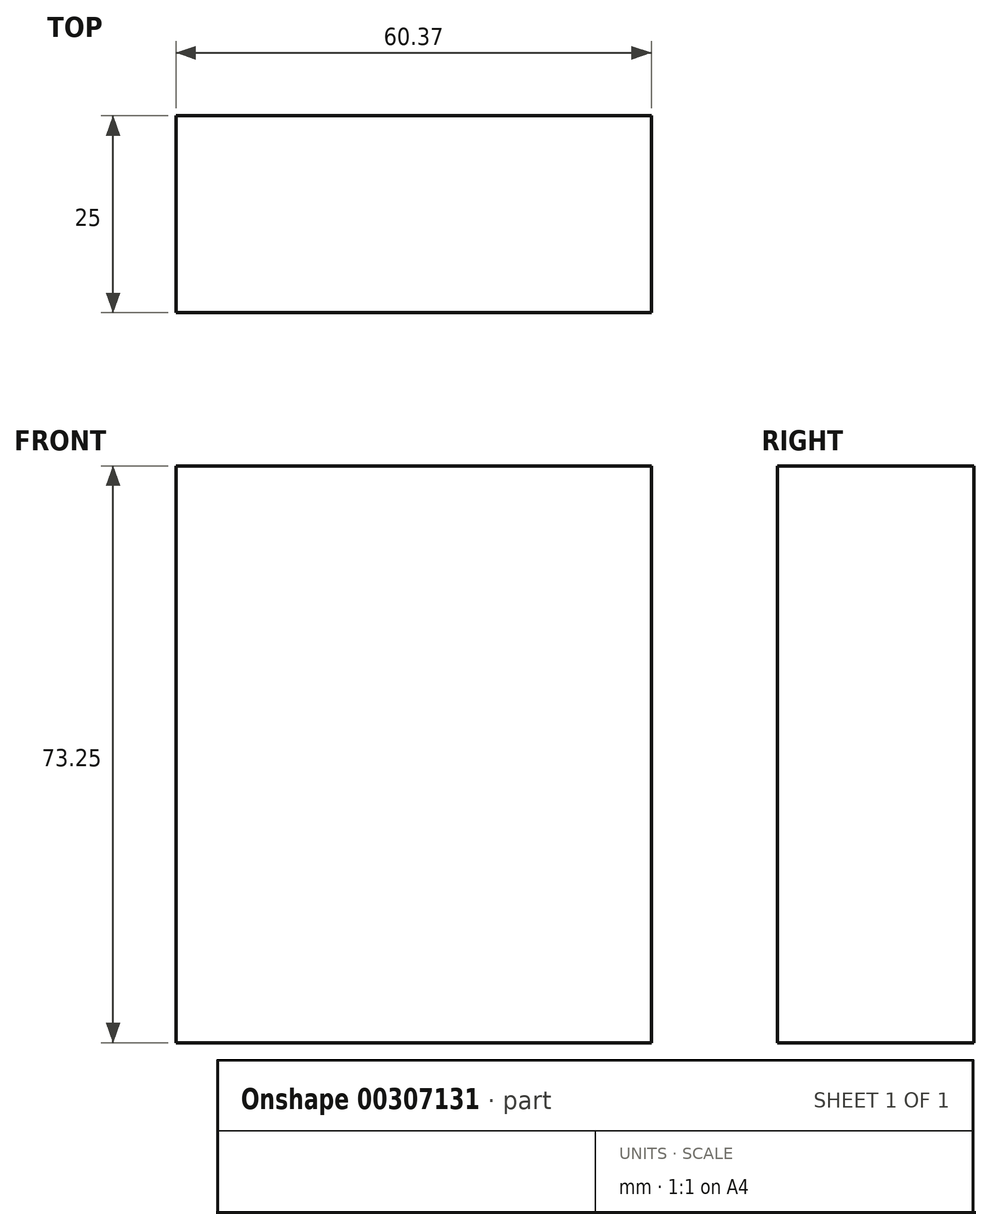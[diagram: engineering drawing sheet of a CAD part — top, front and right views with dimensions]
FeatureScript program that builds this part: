
annotation { "Feature Type Name" : "Feature", "Feature Type Description" : "" }
export const myFeature = defineFeature(function(context is Context, id is Id, definition is map)
    precondition{}
    {
        {
            var Q0;
            Q0=qCreatedBy(makeId("Front.planeOp"),FACE);
            var sketch = newSketch(context, id + "F0", { "sketchPlane" : qUnion([Q0])});
            skLineSegment(sketch, "E0.bottom", {"start": v(-95.1, 6.95) * mm, "end": v(-34.73, 6.95) * mm});
            skLineSegment(sketch, "E0.top", {"start": v(-95.1, 80.2) * mm, "end": v(-34.73, 80.2) * mm});
            skLineSegment(sketch, "E0.left", {"start": v(-95.1, 6.95) * mm, "end": v(-95.1, 80.2) * mm});
            skLineSegment(sketch, "E0.right", {"start": v(-34.73, 6.95) * mm, "end": v(-34.73, 80.2) * mm});
            skPoint(sketch, "E0.middle", {"position": v(-64.91, 43.58) * mm});
            skSolve(sketch);
        }
        {
            var Q0;
            Q0=makeQuery(id+"F0.imprint","IMPRINT",FACE,{"disambiguationData":[TD([[makeQuery(id+"F0.imprint","IMPRINT",EDGE,{"derivedFrom":sQuery(id+"F0.wireOp",EDGE,"E0.bottom")}),1.0]])]});
            extrude(context, id + "F1", {"entities" : qUnion([Q0]), "depth" : 25 * mm});
        }
    });
